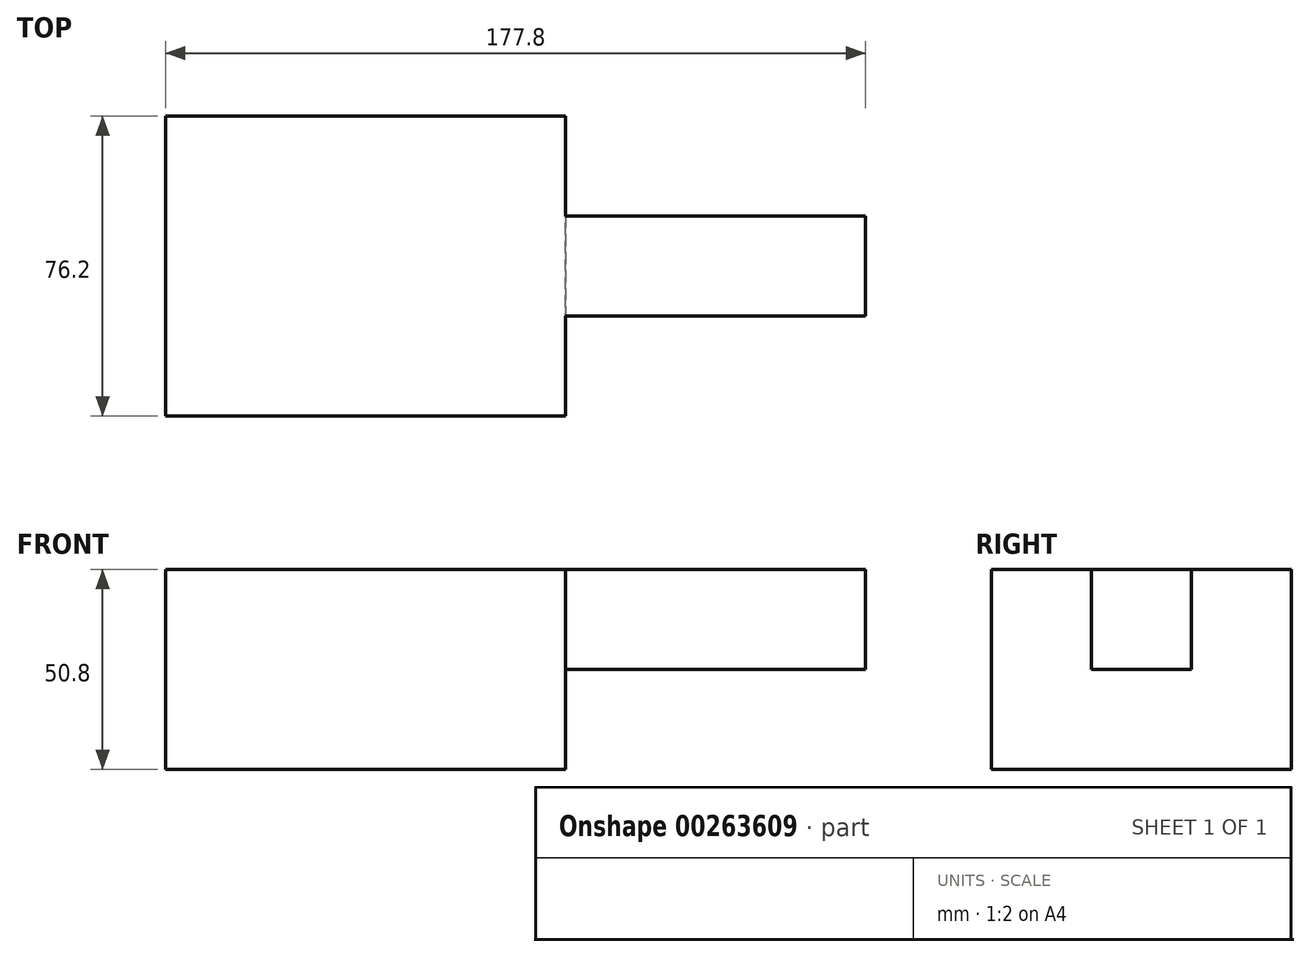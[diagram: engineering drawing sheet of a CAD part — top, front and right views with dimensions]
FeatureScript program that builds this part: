
annotation { "Feature Type Name" : "Feature", "Feature Type Description" : "" }
export const myFeature = defineFeature(function(context is Context, id is Id, definition is map)
    precondition{}
    {
        {
            var Q0;
            Q0=qCreatedBy(makeId("Front.planeOp"),FACE);
            var sketch = newSketch(context, id + "F0", { "sketchPlane" : qUnion([Q0])});
            skLineSegment(sketch, "E0.bottom", {"start": v(-74.85, 73.98) * mm, "end": v(26.75, 73.98) * mm});
            skLineSegment(sketch, "E0.top", {"start": v(-74.85, 23.18) * mm, "end": v(26.75, 23.18) * mm});
            skLineSegment(sketch, "E0.left", {"start": v(-74.85, 73.98) * mm, "end": v(-74.85, 23.18) * mm});
            skLineSegment(sketch, "E0.right", {"start": v(26.75, 73.98) * mm, "end": v(26.75, 23.18) * mm});
            skSolve(sketch);
        }
        {
            var Q0;
            Q0=makeQuery(id+"F0.imprint","IMPRINT",FACE,{"disambiguationData":[TD([[makeQuery(id+"F0.imprint","IMPRINT",EDGE,{"derivedFrom":sQuery(id+"F0.wireOp",EDGE,"E0.bottom")}),-1.0]])]});
            extrude(context, id + "F1", {"entities" : qUnion([Q0]), "depth" : 76.2 * mm});
        }
        {
            var Q0;
            Q0=makeQuery(id+"F1.opExtrude","SWEPT_FACE",FACE,{"disambiguationData":[OSD([sQuery(id+"F0.wireOp",EDGE,"E0.right")])]});
            var sketch = newSketch(context, id + "F2", { "sketchPlane" : qUnion([Q0])});
            skLineSegment(sketch, "E1", {"start": v(-25.4, 73.98) * mm, "end": v(-25.4, 48.58) * mm});
            skLineSegment(sketch, "E2", {"start": v(-25.4, 48.58) * mm, "end": v(-50.8, 48.58) * mm});
            skLineSegment(sketch, "E3", {"start": v(-50.8, 48.58) * mm, "end": v(-50.8, 73.98) * mm});
            skLineSegment(sketch, "E4", {"start": v(-50.8, 73.98) * mm, "end": v(-25.4, 73.98) * mm});
            skSolve(sketch);
        }
        {
            var Q0;
            Q0=makeQuery(id+"F2.imprint","IMPRINT",FACE,{"disambiguationData":[TD([[makeQuery(id+"F2.imprint","IMPRINT",EDGE,{"derivedFrom":sQuery(id+"F2.wireOp",EDGE,"E1")}),-1.0]])]});
            extrude(context, id + "F3", {"entities" : qUnion([Q0]), "operationType" : NewBodyOperationType.ADD, "depth" : 76.2 * mm});
        }
    });
